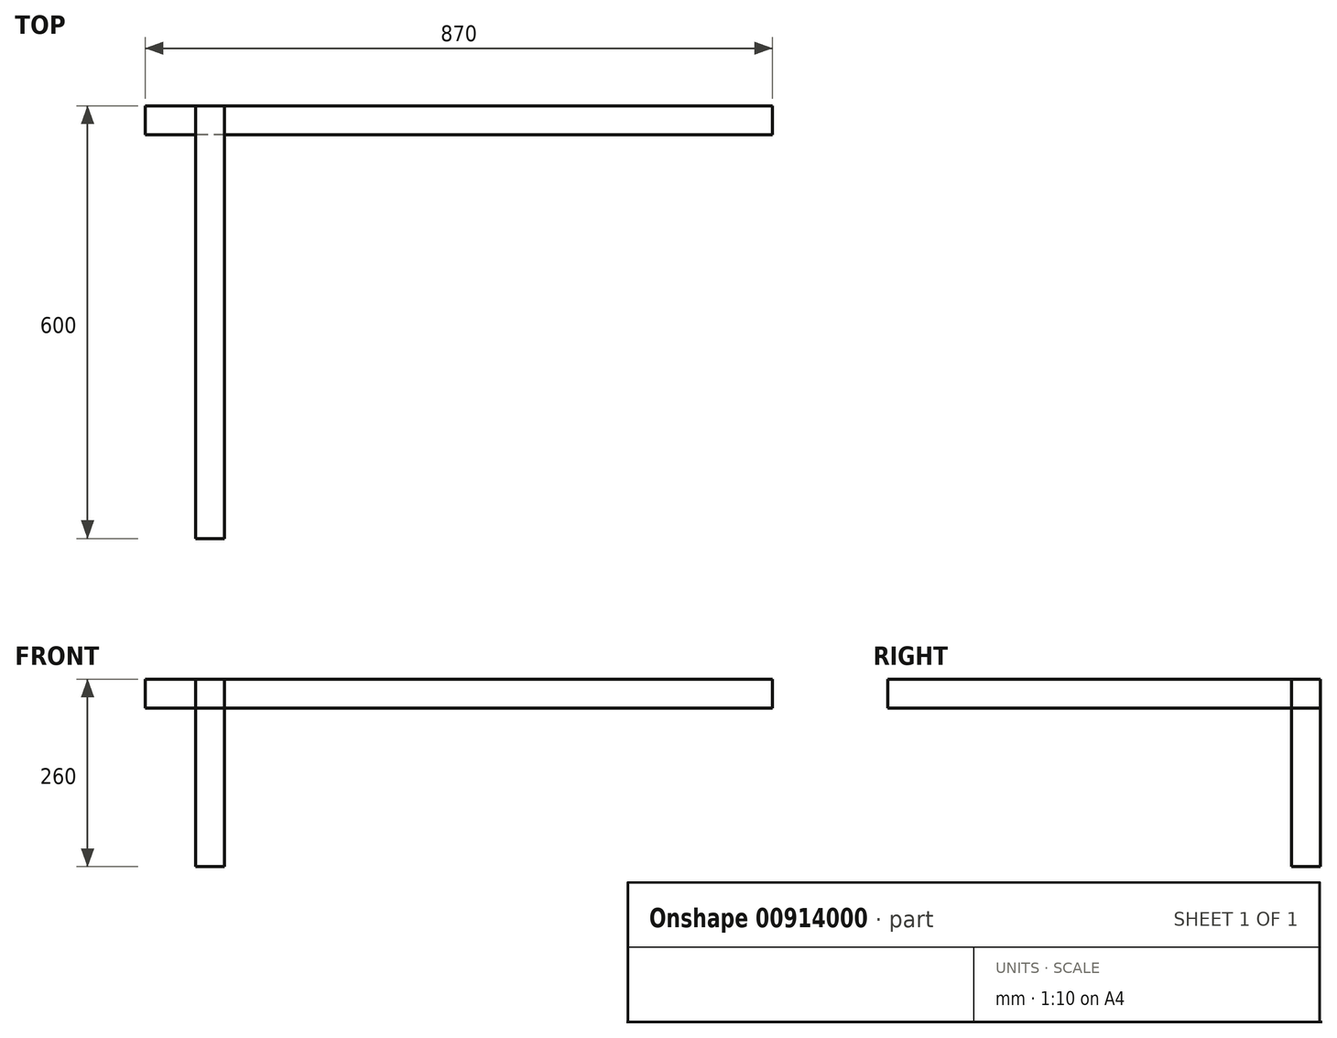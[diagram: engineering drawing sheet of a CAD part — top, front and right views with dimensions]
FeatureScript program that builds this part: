
annotation { "Feature Type Name" : "Feature", "Feature Type Description" : "" }
export const myFeature = defineFeature(function(context is Context, id is Id, definition is map)
    precondition{}
    {
        {
            var Q0;
            Q0=qCreatedBy(makeId("Top.planeOp"),FACE);
            var sketch = newSketch(context, id + "F0", { "sketchPlane" : qUnion([Q0])});
            skLineSegment(sketch, "E0.bottom", {"start": v(-380, 260) * mm, "end": v(380, 260) * mm});
            skLineSegment(sketch, "E0.top", {"start": v(-380, -260) * mm, "end": v(380, -260) * mm});
            skLineSegment(sketch, "E0.left", {"start": v(-380, 260) * mm, "end": v(-380, -260) * mm});
            skLineSegment(sketch, "E0.right", {"start": v(380, 260) * mm, "end": v(380, -260) * mm});
            skLineSegment(sketch, "E1", {"start": v(-380, 260) * mm, "end": v(380, -260) * mm, "construction": true});
            skLineSegment(sketch, "E2", {"start": v(-380, 260) * mm, "end": v(-380, 300) * mm});
            skLineSegment(sketch, "E3", {"start": v(-380, 300) * mm, "end": v(-420, 300) * mm});
            skLineSegment(sketch, "E4", {"start": v(-420, 300) * mm, "end": v(-420, -300) * mm});
            skLineSegment(sketch, "E5", {"start": v(-420, -300) * mm, "end": v(-380, -300) * mm});
            skLineSegment(sketch, "E6", {"start": v(-380, -300) * mm, "end": v(-380, -260) * mm});
            skLineSegment(sketch, "E7", {"start": v(-380, 300) * mm, "end": v(380, 300) * mm});
            skLineSegment(sketch, "E8", {"start": v(380, 300) * mm, "end": v(380, 260) * mm});
            skLineSegment(sketch, "E9", {"start": v(-380, -300) * mm, "end": v(380, -300) * mm});
            skLineSegment(sketch, "E10", {"start": v(380, -300) * mm, "end": v(380, -260) * mm});
            skLineSegment(sketch, "E11", {"start": v(380, 300) * mm, "end": v(420, 300) * mm});
            skLineSegment(sketch, "E12", {"start": v(420, 300) * mm, "end": v(420, -300) * mm});
            skLineSegment(sketch, "E13", {"start": v(420, -300) * mm, "end": v(380, -300) * mm});
            skSolve(sketch);
        }
        {
            var Q0;
            Q0=makeQuery(id+"F0.imprint","IMPRINT",FACE,{"disambiguationData":[TD([[makeQuery(id+"F0.imprint","IMPRINT",EDGE,{"derivedFrom":sQuery(id+"F0.wireOp",EDGE,"E0.left")}),-1.0]])]});
            extrude(context, id + "F1", {"entities" : qUnion([Q0]), "depth" : 40 * mm, "offsetDistance" : 25 * mm});
        }
        {
            var Q0;
            Q0=makeQuery(id+"F0.imprint","IMPRINT",FACE,{"disambiguationData":[TD([[makeQuery(id+"F0.imprint","IMPRINT",EDGE,{"derivedFrom":sQuery(id+"F0.wireOp",EDGE,"E0.bottom")}),1.0]])]});
            var Q1;
            Q1=makeQuery(id+"F1.opExtrude","CAP_FACE",FACE,{"disambiguationData":[OSD([sQuery(id+"F0.wireOp",EDGE,"E0.left"),sQuery(id+"F0.wireOp",EDGE,"E2"),sQuery(id+"F0.wireOp",EDGE,"E3"),sQuery(id+"F0.wireOp",EDGE,"E4"),sQuery(id+"F0.wireOp",EDGE,"E5"),sQuery(id+"F0.wireOp",EDGE,"E6")])],"isStart":false});
            extrude(context, id + "F2", {"entities" : qUnion([Q0]), "endBound" : BoundingType.UP_TO_SURFACE, "depth" : 25 * mm, "endBoundEntityFace" : qUnion([Q1]), "offsetDistance" : 25 * mm});
        }
        {
            var Q0;
            Q0=makeQuery(id+"F2.opExtrude","CAP_FACE",FACE,{"disambiguationData":[OSD([sQuery(id+"F0.wireOp",EDGE,"E0.bottom"),sQuery(id+"F0.wireOp",EDGE,"E2"),sQuery(id+"F0.wireOp",EDGE,"E7"),sQuery(id+"F0.wireOp",EDGE,"E8")])],"isStart":true});
            var sketch = newSketch(context, id + "F3", { "sketchPlane" : qUnion([Q0])});
            skLineSegment(sketch, "E14.bottom", {"start": v(-380, -300) * mm, "end": v(-420, -300) * mm});
            skLineSegment(sketch, "E14.top", {"start": v(-380, -260) * mm, "end": v(-420, -260) * mm});
            skLineSegment(sketch, "E14.left", {"start": v(-380, -300) * mm, "end": v(-380, -260) * mm});
            skLineSegment(sketch, "E14.right", {"start": v(-420, -300) * mm, "end": v(-420, -260) * mm});
            skLineSegment(sketch, "E15.0", {"start": v(-420, -300) * mm, "end": v(-420, 300) * mm, "construction": true});
            skLineSegment(sketch, "E16.0", {"start": v(-380, -260) * mm, "end": v(380, -260) * mm, "construction": true});
            skSolve(sketch);
        }
        {
            var Q0;
            Q0 = qSketchRegion(id + "F3", true);
            extrude(context, id + "F4", {"entities" : qUnion([Q0]), "depth" : 220 * mm, "offsetDistance" : 25 * mm});
        }
        {
            var Q0;
            Q0=makeQuery(id+"F1.opExtrude","SWEPT_FACE",FACE,{"disambiguationData":[OSD([sQuery(id+"F0.wireOp",EDGE,"E4")])]});
            var sketch = newSketch(context, id + "F5", { "sketchPlane" : qUnion([Q0])});
            skLineSegment(sketch, "E17.bottom", {"start": v(-300, 40) * mm, "end": v(-260, 40) * mm});
            skLineSegment(sketch, "E17.top", {"start": v(-300, 0) * mm, "end": v(-260, 0) * mm});
            skLineSegment(sketch, "E17.left", {"start": v(-300, 40) * mm, "end": v(-300, 0) * mm});
            skLineSegment(sketch, "E17.right", {"start": v(-260, 40) * mm, "end": v(-260, 0) * mm});
            skSolve(sketch);
        }
        {
            var Q0;
            Q0 = qSketchRegion(id + "F5", true);
            extrude(context, id + "F6", {"entities" : qUnion([Q0]), "depth" : 70 * mm, "offsetDistance" : 25 * mm});
        }
    });
